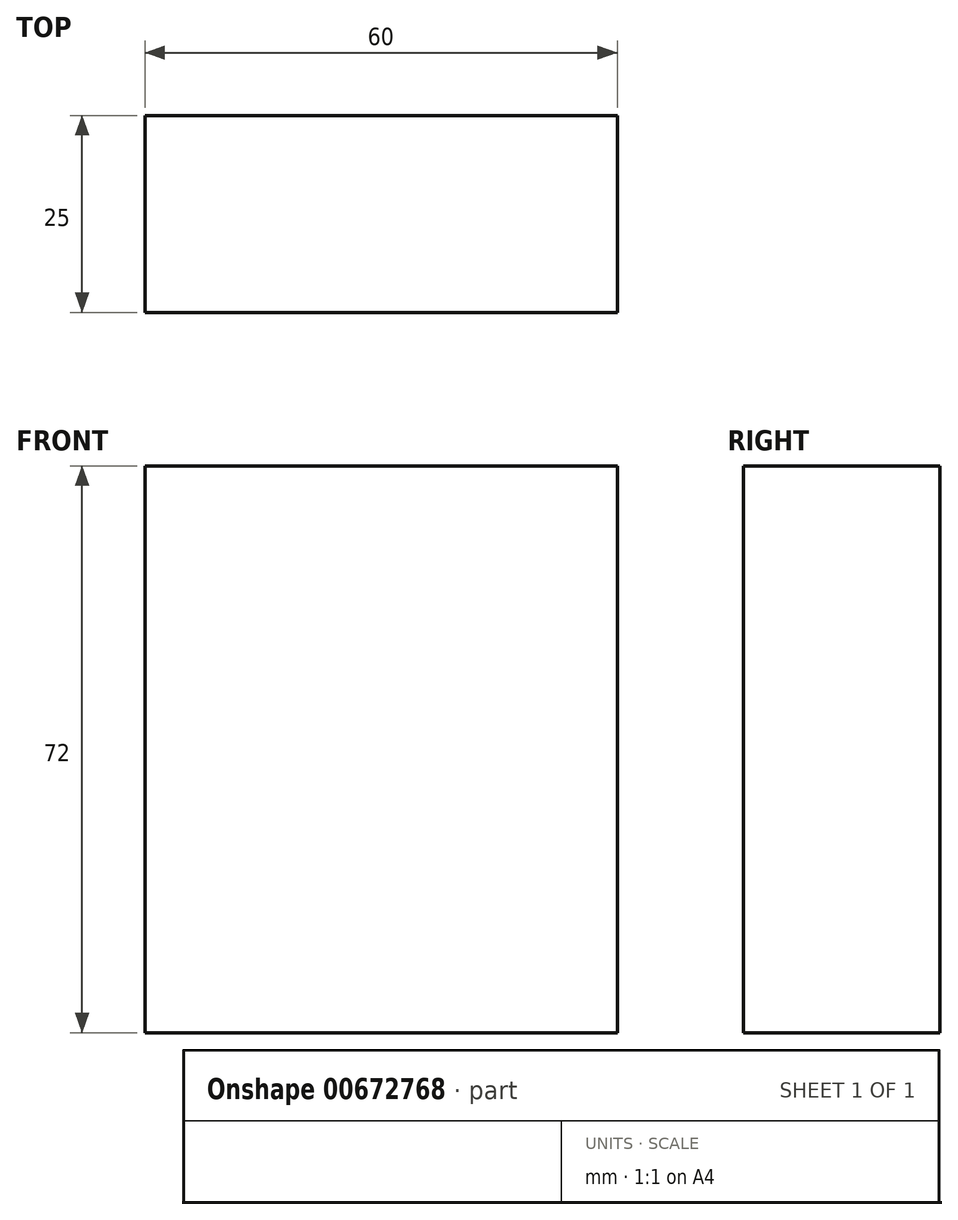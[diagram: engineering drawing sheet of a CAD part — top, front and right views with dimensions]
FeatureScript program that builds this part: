
annotation { "Feature Type Name" : "Feature", "Feature Type Description" : "" }
export const myFeature = defineFeature(function(context is Context, id is Id, definition is map)
    precondition{}
    {
        {
            var Q0;
            Q0=qCreatedBy(makeId("Front.planeOp"),FACE);
            var sketch = newSketch(context, id + "F0", { "sketchPlane" : qUnion([Q0])});
            skLineSegment(sketch, "E0.bottom", {"start": v(30, -36) * mm, "end": v(-30, -36) * mm});
            skLineSegment(sketch, "E0.top", {"start": v(30, 36) * mm, "end": v(-30, 36) * mm});
            skLineSegment(sketch, "E0.left", {"start": v(30, -36) * mm, "end": v(30, 36) * mm});
            skLineSegment(sketch, "E0.right", {"start": v(-30, -36) * mm, "end": v(-30, 36) * mm});
            skPoint(sketch, "E0.middle", {"position": v(0, 0) * mm});
            skSolve(sketch);
        }
        {
            var Q0;
            Q0=makeQuery(id+"F0.imprint","IMPRINT",FACE,{"disambiguationData":[TD([[makeQuery(id+"F0.imprint","IMPRINT",EDGE,{"derivedFrom":sQuery(id+"F0.wireOp",EDGE,"E0.bottom")}),-1.0]])]});
            extrude(context, id + "F1", {"entities" : qUnion([Q0]), "depth" : 25 * mm, "offsetDistance" : 25 * mm});
        }
    });
